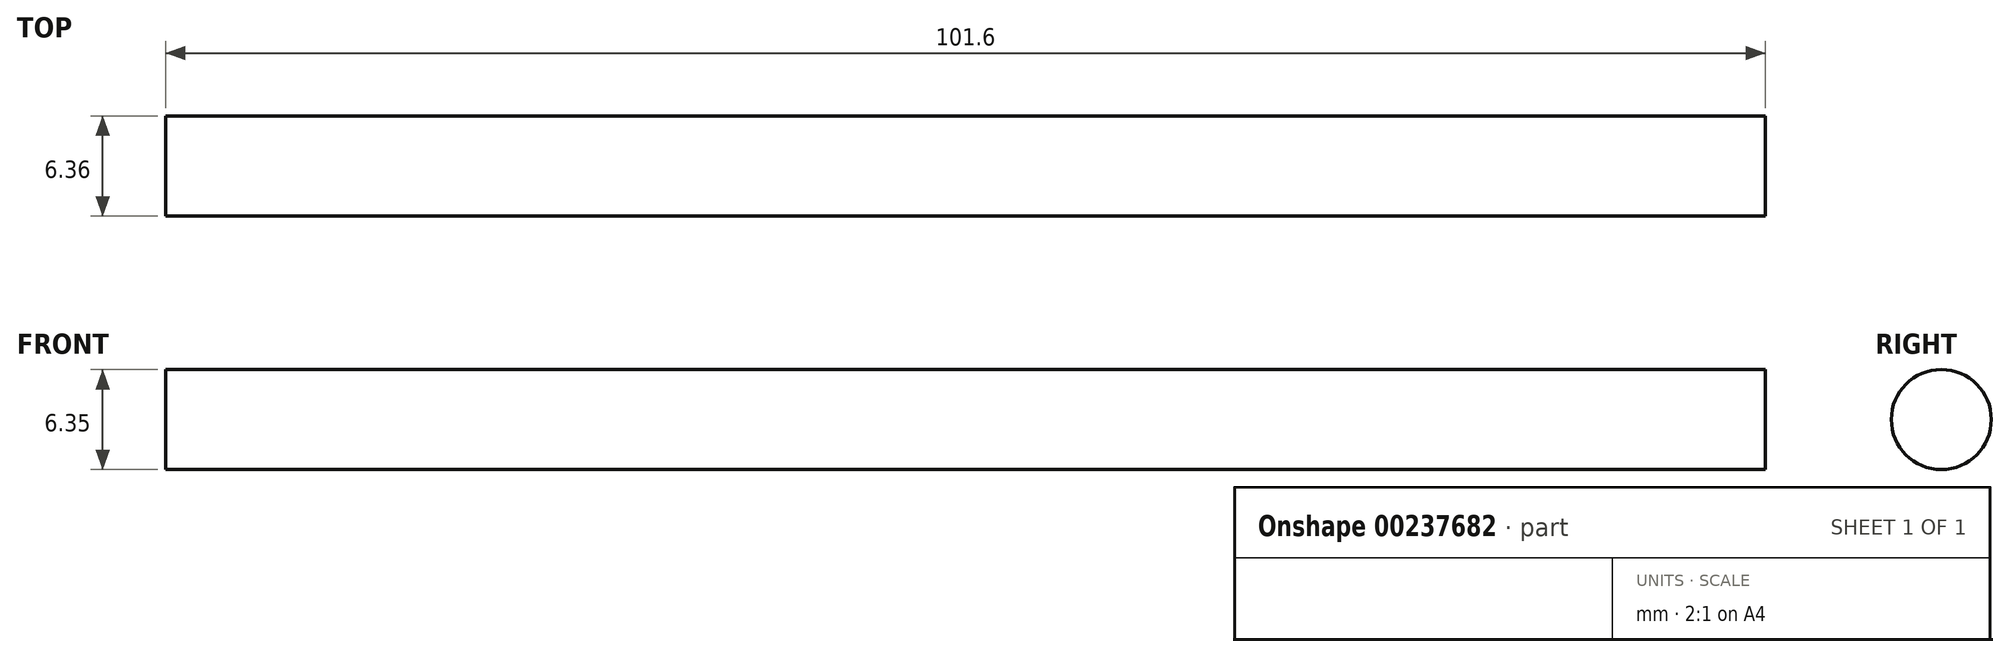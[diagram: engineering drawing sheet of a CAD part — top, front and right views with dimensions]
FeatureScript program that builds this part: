
annotation { "Feature Type Name" : "Feature", "Feature Type Description" : "" }
export const myFeature = defineFeature(function(context is Context, id is Id, definition is map)
    precondition{}
    {
        {
            var Q0;
            Q0=qCreatedBy(makeId("Right.planeOp"),FACE);
            var sketch = newSketch(context, id + "F0", { "sketchPlane" : qUnion([Q0])});
            skCircle(sketch, "E0", {"center": v(0, -0.3) * mm, "radius": 3.18 * mm});
            skSolve(sketch);
        }
        {
            var Q0;
            Q0 = qSketchRegion(id + "F0", true);
            extrude(context, id + "F1", {"entities" : qUnion([Q0]), "depth" : 101.6 * mm});
        }
    });
